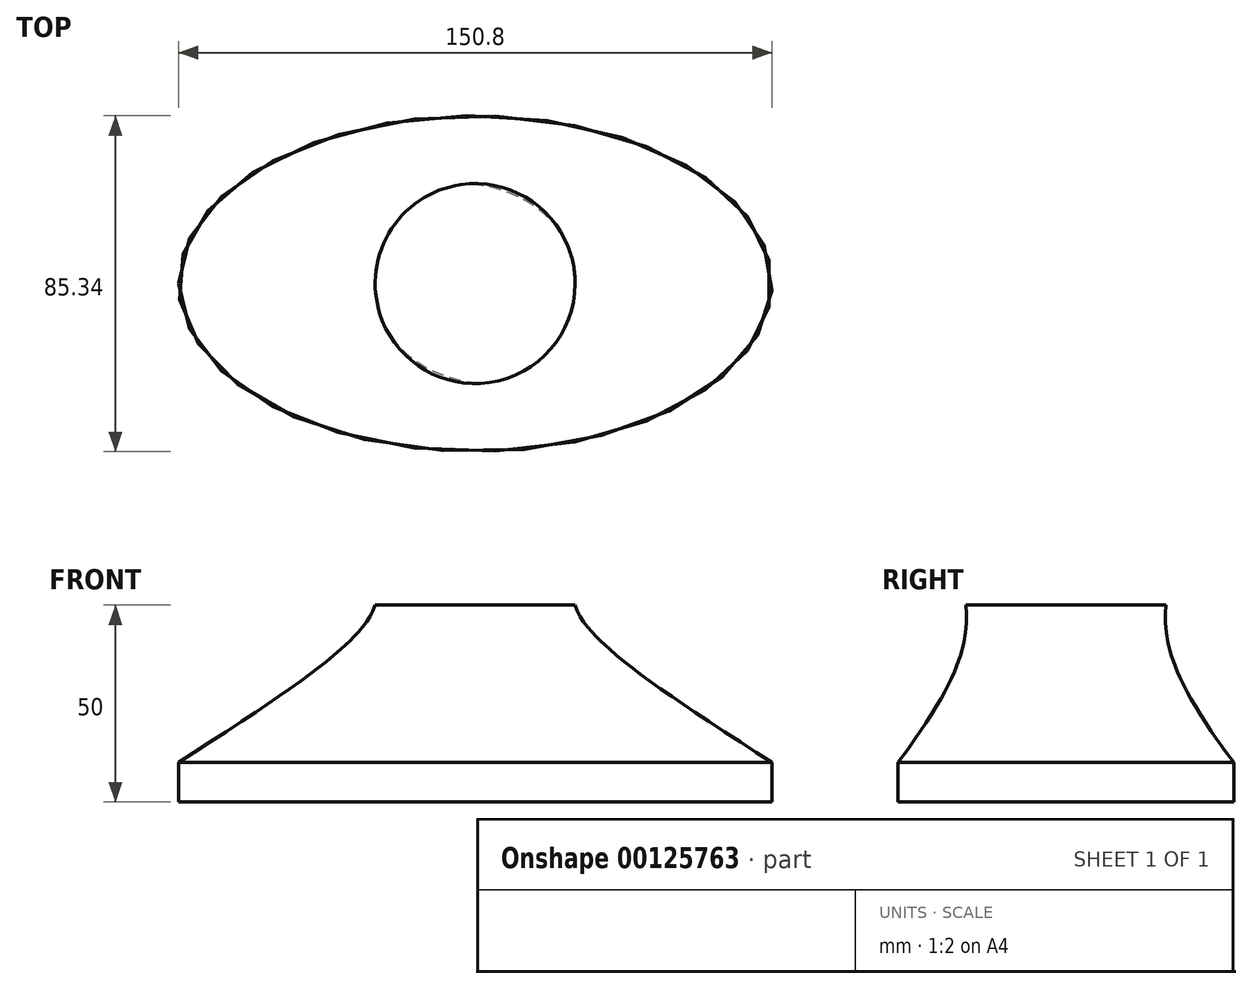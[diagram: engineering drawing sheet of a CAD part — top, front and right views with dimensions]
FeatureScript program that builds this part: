
annotation { "Feature Type Name" : "Feature", "Feature Type Description" : "" }
export const myFeature = defineFeature(function(context is Context, id is Id, definition is map)
    precondition{}
    {
        {
            var Q0;
            Q0=qCreatedBy(makeId("Top.planeOp"),FACE);
            cPlane(context, id + "F0", {"entities" : qUnion([Q0]), "cplaneType" : CPlaneType.OFFSET, "offset" : 40 * mm, "width" : 152.4 * mm, "height" : 152.4 * mm});
        }
        {
            var Q0;
            Q0=qCreatedBy(id+"F0.planeOp",FACE);
            var sketch = newSketch(context, id + "F1", { "sketchPlane" : qUnion([Q0])});
            skCircle(sketch, "E0", {"center": v(0, 0) * mm, "radius": 25.4 * mm});
            skSolve(sketch);
        }
        {
            var Q0;
            Q0=qCreatedBy(makeId("Top.planeOp"),FACE);
            var sketch = newSketch(context, id + "F2", { "sketchPlane" : qUnion([Q0])});
            skEllipse(sketch, "E1", {"center": v(0, 0) * mm, "majorRadius": 42.67 * mm, "minorRadius": 75.4 * mm, "majorAxis": v(0, 1)});
            skSolve(sketch);
        }
        {
            var Q0;
            Q0 = qSketchRegion(id + "F2", true);
            extrude(context, id + "F3", {"entities" : qUnion([Q0]), "oppositeDirection" : true, "depth" : 10 * mm});
        }
        {
            var Q0;
            Q0=makeQuery(id+"F1.imprint","IMPRINT",FACE,{"disambiguationData":[TD([[makeQuery(id+"F1.imprint","IMPRINT",EDGE,{"derivedFrom":sQuery(id+"F1.wireOp",EDGE,"E0")}),1.0]])]});
            var Q1;
            Q1=makeQuery(id+"F3.opExtrude","CAP_FACE",FACE,{"disambiguationData":[OSD([sQuery(id+"F2.wireOp",EDGE,"E1")])],"isStart":true});
            loft(context, id + "F4", {"sheetProfilesArray" : [{ "sheetProfileEntities" : qUnion([Q0]) }, { "sheetProfileEntities" : qUnion([Q1]) }]});
        }
    });
